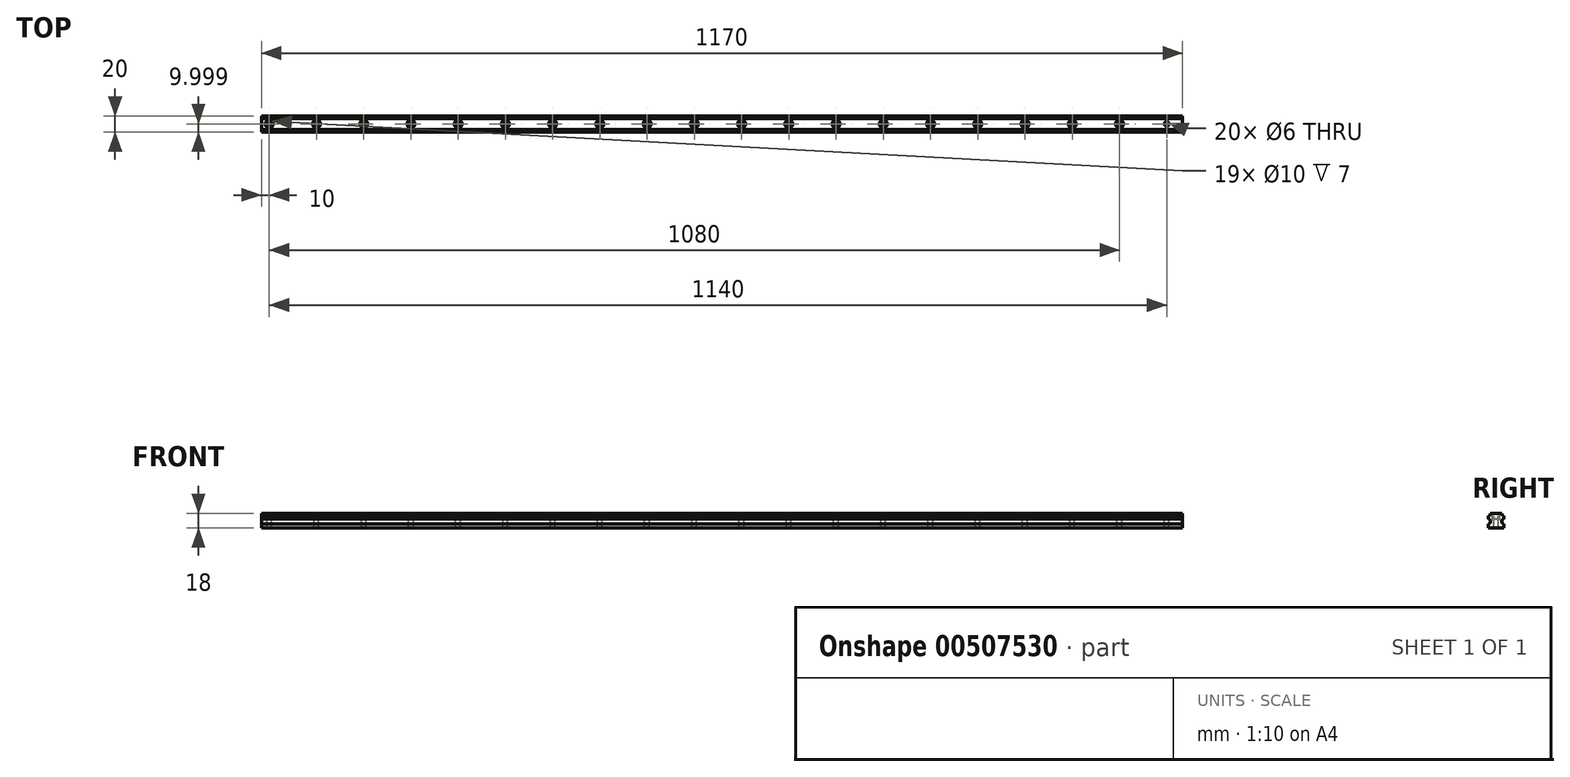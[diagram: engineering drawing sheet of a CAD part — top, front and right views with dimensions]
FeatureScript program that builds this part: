
annotation { "Feature Type Name" : "Feature", "Feature Type Description" : "" }
export const myFeature = defineFeature(function(context is Context, id is Id, definition is map)
    precondition{}
    {
        {
            var Q0;
            Q0=qCreatedBy(makeId("Right.planeOp"),FACE);
            var sketch = newSketch(context, id + "F0", { "sketchPlane" : qUnion([Q0])});
            skLineSegment(sketch, "E0", {"start": v(-26.04, 0) * mm, "end": v(-26.04, 5) * mm});
            skLineSegment(sketch, "E1", {"start": v(-26.04, 11) * mm, "end": v(-26.04, 15) * mm});
            skLineSegment(sketch, "E2", {"start": v(-23.04, 18) * mm, "end": v(-9.04, 18) * mm});
            skLineSegment(sketch, "E3", {"start": v(-6.04, 15) * mm, "end": v(-6.04, 11) * mm});
            skLineSegment(sketch, "E4", {"start": v(-6.04, 5) * mm, "end": v(-6.04, 0) * mm});
            skLineSegment(sketch, "E5", {"start": v(-6.04, 0) * mm, "end": v(-26.04, 0) * mm});
            skArc(sketch, "E6", {"start": v(-26.04, 5) * mm, "mid": v(-23.04, 8) * mm, "end": v(-26.04, 11) * mm});
            skArc(sketch, "E7", {"start": v(-6.04, 11) * mm, "mid": v(-9.04, 8) * mm, "end": v(-6.04, 5) * mm});
            skArc(sketch, "E8", {"start": v(-26.04, 15) * mm, "mid": v(-23.92, 15.88) * mm, "end": v(-23.04, 18) * mm});
            skArc(sketch, "E9", {"start": v(-9.04, 18) * mm, "mid": v(-8.16, 15.88) * mm, "end": v(-6.04, 15) * mm});
            skSolve(sketch);
        }
        {
            var Q0;
            Q0 = qSketchRegion(id + "F0", true);
            extrude(context, id + "F1", {"entities" : qUnion([Q0]), "offsetDistance" : 25 * mm, "depth" : 1170 * mm});
        }
        {
            var Q0;
            Q0=makeQuery(id+"F1.opExtrude","SWEPT_FACE",FACE,{"disambiguationData":[OSD([sQuery(id+"F0.wireOp",EDGE,"E2")])]});
            var sketch = newSketch(context, id + "F2", { "sketchPlane" : qUnion([Q0])});
            skCircle(sketch, "E10", {"center": v(10, -16.04) * mm, "radius": 3 * mm});
            skCircle(sketch, "E11", {"center": v(70, -16.04) * mm, "radius": 3 * mm});
            skCircle(sketch, "E12", {"center": v(130, -16.04) * mm, "radius": 3 * mm});
            skCircle(sketch, "E13", {"center": v(190, -16.04) * mm, "radius": 3 * mm});
            skCircle(sketch, "E14", {"center": v(250, -16.04) * mm, "radius": 3 * mm});
            skCircle(sketch, "E15", {"center": v(310, -16.04) * mm, "radius": 3 * mm});
            skCircle(sketch, "E16", {"center": v(370, -16.04) * mm, "radius": 3 * mm});
            skCircle(sketch, "E17", {"center": v(430, -16.04) * mm, "radius": 3 * mm});
            skCircle(sketch, "E18", {"center": v(490, -16.04) * mm, "radius": 3 * mm});
            skCircle(sketch, "E19", {"center": v(550, -16.04) * mm, "radius": 3 * mm});
            skCircle(sketch, "E20", {"center": v(610, -16.04) * mm, "radius": 3 * mm});
            skCircle(sketch, "E21", {"center": v(670, -16.04) * mm, "radius": 3 * mm});
            skCircle(sketch, "E22", {"center": v(730, -16.04) * mm, "radius": 3 * mm});
            skCircle(sketch, "E23", {"center": v(790, -16.04) * mm, "radius": 3 * mm});
            skCircle(sketch, "E24", {"center": v(850, -16.04) * mm, "radius": 3 * mm});
            skCircle(sketch, "E25", {"center": v(910, -16.04) * mm, "radius": 3 * mm});
            skCircle(sketch, "E26", {"center": v(970, -16.04) * mm, "radius": 3 * mm});
            skCircle(sketch, "E27", {"center": v(1030, -16.04) * mm, "radius": 3 * mm});
            skCircle(sketch, "E28", {"center": v(1090, -16.04) * mm, "radius": 3 * mm});
            skCircle(sketch, "E29", {"center": v(1150, -16.04) * mm, "radius": 3 * mm});
            skCircle(sketch, "E30", {"center": v(1210, -16.04) * mm, "radius": 3 * mm});
            skCircle(sketch, "E31", {"center": v(1270, -16.04) * mm, "radius": 3 * mm});
            skCircle(sketch, "E32", {"center": v(1330, -16.04) * mm, "radius": 3 * mm});
            skCircle(sketch, "E33", {"center": v(1390, -16.04) * mm, "radius": 3 * mm});
            skCircle(sketch, "E34", {"center": v(1450, -16.04) * mm, "radius": 3 * mm});
            skCircle(sketch, "E35", {"center": v(1510, -16.04) * mm, "radius": 3 * mm});
            skCircle(sketch, "E36", {"center": v(1570, -16.04) * mm, "radius": 3 * mm});
            skCircle(sketch, "E37", {"center": v(1630, -16.04) * mm, "radius": 3 * mm});
            skCircle(sketch, "E38", {"center": v(1690, -16.04) * mm, "radius": 3 * mm});
            skCircle(sketch, "E39", {"center": v(1750, -16.04) * mm, "radius": 3 * mm});
            skCircle(sketch, "E40", {"center": v(1810, -16.04) * mm, "radius": 3 * mm});
            skCircle(sketch, "E41", {"center": v(1870, -16.04) * mm, "radius": 3 * mm});
            skCircle(sketch, "E42", {"center": v(1930, -16.04) * mm, "radius": 3 * mm});
            skCircle(sketch, "E43", {"center": v(1990, -16.04) * mm, "radius": 3 * mm});
            skSolve(sketch);
        }
        {
            var Q0;
            Q0 = qSketchRegion(id + "F2", true);
            extrude(context, id + "F3", {"entities" : qUnion([Q0]), "operationType" : NewBodyOperationType.REMOVE, "oppositeDirection" : true, "depth" : 18 * mm});
        }
        {
            var Q0;
            Q0=makeQuery(id+"F1.opExtrude","SWEPT_FACE",FACE,{"disambiguationData":[OSD([sQuery(id+"F0.wireOp",EDGE,"E2")])]});
            var sketch = newSketch(context, id + "F4", { "sketchPlane" : qUnion([Q0])});
            skCircle(sketch, "E44", {"center": v(10, -16.04) * mm, "radius": 5 * mm});
            skCircle(sketch, "E45", {"center": v(70, -16.04) * mm, "radius": 5 * mm});
            skCircle(sketch, "E46", {"center": v(130, -16.04) * mm, "radius": 5 * mm});
            skCircle(sketch, "E47", {"center": v(190, -16.04) * mm, "radius": 5 * mm});
            skCircle(sketch, "E48", {"center": v(250, -16.04) * mm, "radius": 5 * mm});
            skCircle(sketch, "E49", {"center": v(310, -16.04) * mm, "radius": 5 * mm});
            skCircle(sketch, "E50", {"center": v(370, -16.04) * mm, "radius": 5 * mm});
            skCircle(sketch, "E51", {"center": v(430, -16.04) * mm, "radius": 5 * mm});
            skCircle(sketch, "E52", {"center": v(490, -16.04) * mm, "radius": 5 * mm});
            skCircle(sketch, "E53", {"center": v(550, -16.04) * mm, "radius": 5 * mm});
            skCircle(sketch, "E54", {"center": v(610, -16.04) * mm, "radius": 5 * mm});
            skCircle(sketch, "E55", {"center": v(670, -16.04) * mm, "radius": 5 * mm});
            skCircle(sketch, "E56", {"center": v(730, -16.04) * mm, "radius": 5 * mm});
            skCircle(sketch, "E57", {"center": v(790, -16.04) * mm, "radius": 5 * mm});
            skCircle(sketch, "E58", {"center": v(850, -16.04) * mm, "radius": 5 * mm});
            skCircle(sketch, "E59", {"center": v(910, -16.04) * mm, "radius": 5 * mm});
            skCircle(sketch, "E60", {"center": v(970, -16.04) * mm, "radius": 5 * mm});
            skCircle(sketch, "E61", {"center": v(1030, -16.04) * mm, "radius": 5 * mm});
            skCircle(sketch, "E62", {"center": v(1090, -16.04) * mm, "radius": 5 * mm});
            skSolve(sketch);
        }
        {
            var Q0;
            Q0 = qSketchRegion(id + "F4", true);
            extrude(context, id + "F5", {"entities" : qUnion([Q0]), "operationType" : NewBodyOperationType.REMOVE, "oppositeDirection" : true, "depth" : 7 * mm});
        }
    });
